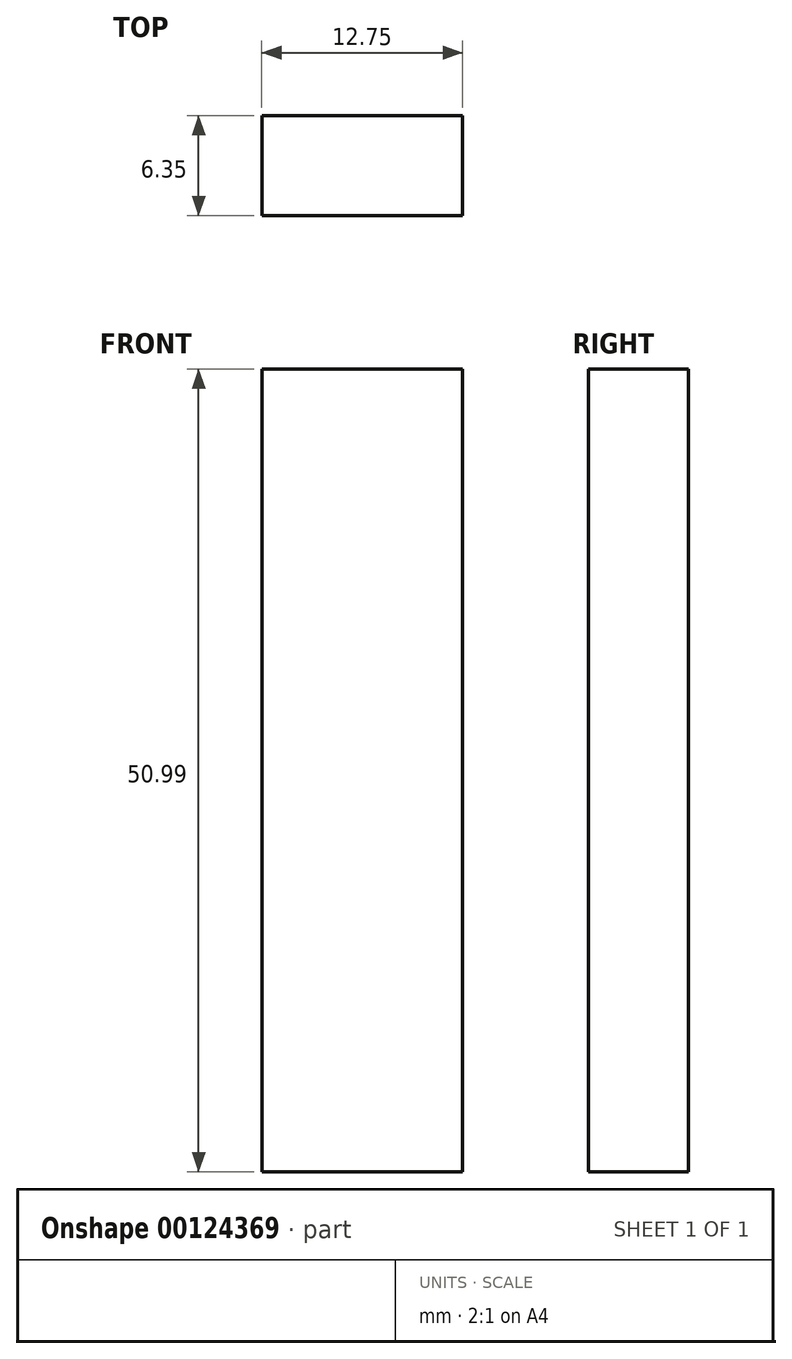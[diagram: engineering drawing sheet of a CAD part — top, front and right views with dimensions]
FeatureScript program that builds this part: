
annotation { "Feature Type Name" : "Feature", "Feature Type Description" : "" }
export const myFeature = defineFeature(function(context is Context, id is Id, definition is map)
    precondition{}
    {
        {
            var Q0;
            Q0=qCreatedBy(makeId("Front.planeOp"),FACE);
            var sketch = newSketch(context, id + "F0", { "sketchPlane" : qUnion([Q0])});
            skLineSegment(sketch, "E0", {"start": v(0, 0) * mm, "end": v(0, 43.12) * mm});
            skLineSegment(sketch, "E1", {"start": v(0, 43.12) * mm, "end": v(25.5, 43.12) * mm});
            skLineSegment(sketch, "E2", {"start": v(25.5, 43.12) * mm, "end": v(25.5, 0) * mm});
            skLineSegment(sketch, "E3", {"start": v(25.5, 0) * mm, "end": v(0, 0) * mm});
            skSolve(sketch);
        }
        {
            var Q0;
            Q0=makeQuery(id+"F0.imprint","IMPRINT",FACE,{"disambiguationData":[TD([[makeQuery(id+"F0.imprint","IMPRINT",EDGE,{"derivedFrom":sQuery(id+"F0.wireOp",EDGE,"E0")}),-1.0]])]});
            extrude(context, id + "F1", {"entities" : qUnion([Q0]), "depth" : 25.4 * mm});
        }
        {
            var Q0;
            Q0=makeQuery(id+"F1.opExtrude","SWEPT_FACE",FACE,{"disambiguationData":[OSD([sQuery(id+"F0.wireOp",EDGE,"E1")])]});
            shell(context, id + "F2", {"entities" : qUnion([Q0]), "thickness" : 2.54 * mm});
        }
        {
            var Q0;
            Q0=makeQuery(id+"F1.opExtrude","SWEPT_BODY",BODY,{"disambiguationData":[OSD([sQuery(id+"F0.wireOp",EDGE,"E0"),sQuery(id+"F0.wireOp",EDGE,"E1"),sQuery(id+"F0.wireOp",EDGE,"E2"),sQuery(id+"F0.wireOp",EDGE,"E3")])]});
            deleteBodies(context, id + "F3", {"entities" : qUnion([Q0])});
        }
        {
            var Q0;
            Q0=qCreatedBy(makeId("Front.planeOp"),FACE);
            var sketch = newSketch(context, id + "F4", { "sketchPlane" : qUnion([Q0])});
            skLineSegment(sketch, "E4", {"start": v(0, 0) * mm, "end": v(-12.75, 0) * mm});
            skLineSegment(sketch, "E5", {"start": v(-12.75, 0) * mm, "end": v(-12.75, 50.99) * mm});
            skLineSegment(sketch, "E6", {"start": v(-12.75, 50.99) * mm, "end": v(0, 50.99) * mm});
            skLineSegment(sketch, "E7", {"start": v(0, 50.99) * mm, "end": v(0, 0) * mm});
            skSolve(sketch);
        }
        {
            var Q0;
            Q0=makeQuery(id+"F4.imprint","IMPRINT",FACE,{"disambiguationData":[TD([[makeQuery(id+"F4.imprint","IMPRINT",EDGE,{"derivedFrom":sQuery(id+"F4.wireOp",EDGE,"E4")}),-1.0]])]});
            extrude(context, id + "F5", {"entities" : qUnion([Q0]), "depth" : 6.35 * mm});
        }
    });
